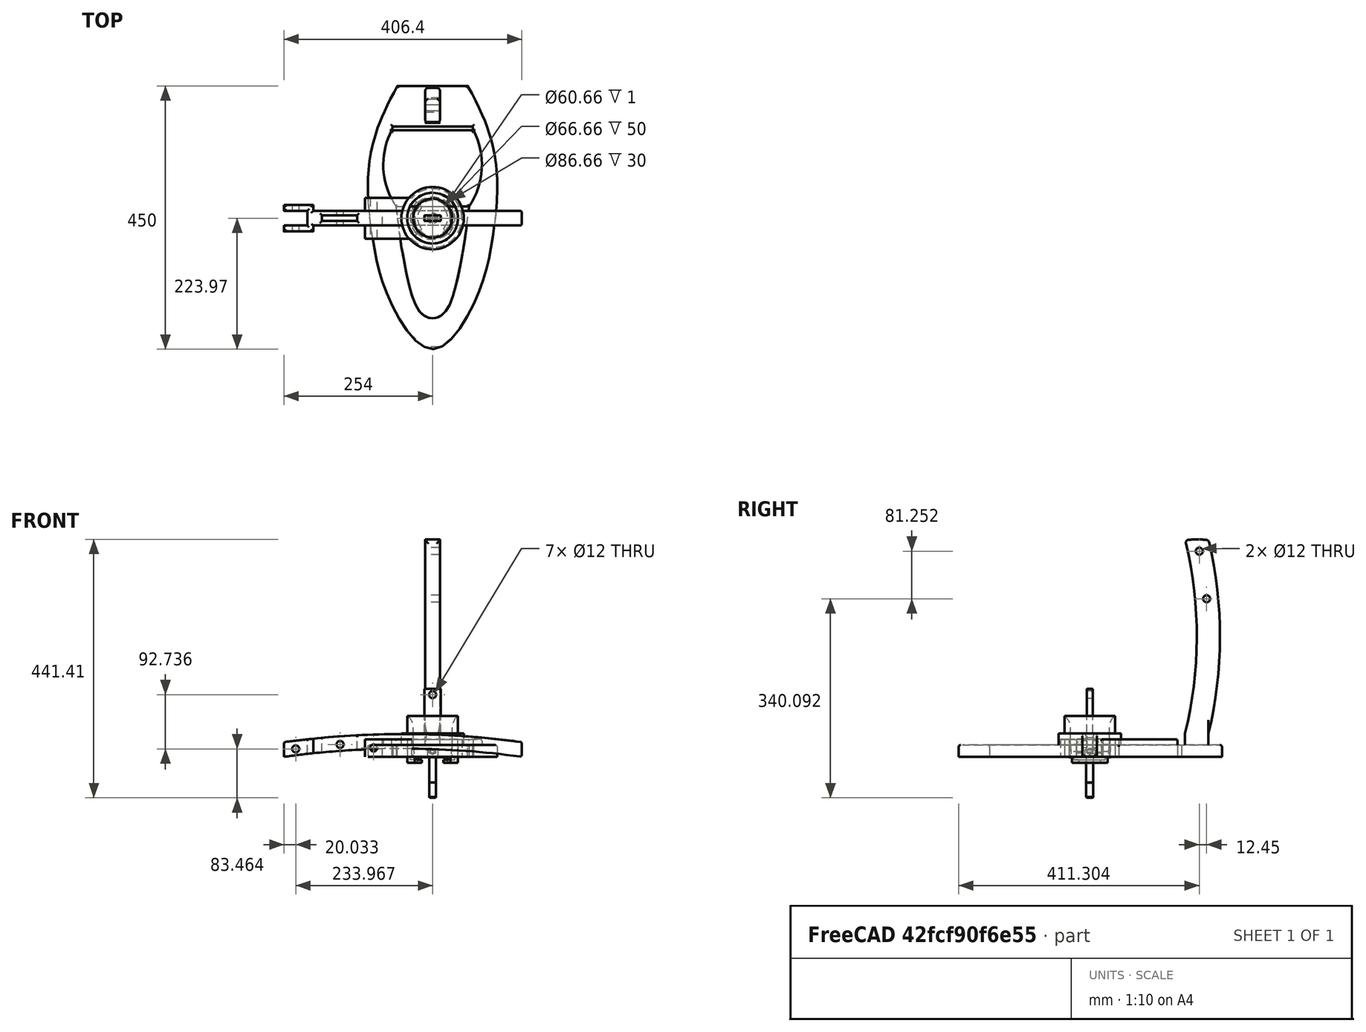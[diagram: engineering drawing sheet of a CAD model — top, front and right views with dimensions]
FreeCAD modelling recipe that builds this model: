
FCSTD DOCUMENT  (FreeCAD 1.0R39109 (Git))
Label: Espresso Machine
License: All rights reserved
LicenseURL: https://en.wikipedia.org/wiki/All_rights_reserved
objects: Sketcher::SketchObject×19, App::FeaturePython×9, PartDesign::Pad×8, App::Link×8, PartDesign::Pocket×6, PartDesign::Revolution×5, PartDesign::Body×5, PartDesign::Fillet×5, Part::FeaturePython×2, PartDesign::Mirrored×1, App::VarSet×1, App::DocumentObjectGroup×1, Assembly::JointGroup×1, Assembly::AssemblyObject×1
note: 119 computed .brp shape members not serialized (recipe doc carries the construction recipe); baked Part::Feature solids carry a one-line shape summary decoded from their .brp

FEATURE [Sketcher::SketchObject] Sketch
  ArcFitTolerance = 1e-06
  AttachmentSupport = -> [XY_Plane]
  FullyConstrained = true
  MakeInternals = false
  MapMode = 5
  sketch-geometry (2):
    g0: Circle CenterX=0 CenterY=0 CenterZ=0 NormalX=0 NormalY=0 NormalZ=1 AngleXU=0 Radius=33.33
    g1: Circle CenterX=0 CenterY=0 CenterZ=0 NormalX=0 NormalY=0 NormalZ=1 AngleXU=0 Radius=43.33
  constraints (4):
    c: Coincident(g0,g-1)
    c: Coincident(g1,g0)
    c: Diameter(g0) = 66.66
    c: Diameter(g1) = 86.66
FEATURE [PartDesign::Pad] Pad
  Direction = (0,0,1)
  Length = 50
  Length2 = 10
  Profile = -> Sketch
  ReferenceAxis = -> Sketch [N_Axis]
  Refine = true
  Suppressed = false
  Type = 0
FEATURE [Sketcher::SketchObject] Sketch001
  ArcFitTolerance = 1e-06
  AttachmentSupport = -> [XZ_Plane]
  ExternalGeometry = -> [Pad]
  FullyConstrained = true
  MakeInternals = false
  MapMode = 5
  Placement = pos=(0,0,0) rot=(1,0,0;1.5708rad)
  sketch-geometry (4):
    g0: LineSegment StartX=33.33 StartY=50 StartZ=0 EndX=43.33 EndY=50 EndZ=0
    g1: LineSegment StartX=43.33 StartY=50 StartZ=0 EndX=43.33 EndY=70 EndZ=0
    g2: ArcOfCircle CenterX=58.33 CenterY=50 CenterZ=0 NormalX=0 NormalY=0 NormalZ=1 AngleXU=0 Radius=25 StartAngle=2.2143 EndAngle=3.14159
    g3: LineSegment [constr] StartX=33.33 StartY=50 StartZ=0 EndX=33.33 EndY=0 EndZ=0
  constraints (11):
    c: Coincident(g0,g-4)
    c: Coincident(g0,g-3)
    c: Coincident(g0,g1)
    c: Vertical(g1)
    c: DistanceY(g1,g1) = 20
    c: Coincident(g2,g0)
    c: Coincident(g2,g1)
    c: Coincident(g3,g0)
    c: PointOnObject(g3,g-1)
    c: Vertical(g3)
    c: Tangent(g3,g2)
FEATURE [PartDesign::Revolution] Revolution
  Angle = 360
  Angle2 = 60
  Axis = (0,2e-16,1)
  Base = (0,0,0)
  BaseFeature = -> Pad
  Profile = -> Sketch001
  ReferenceAxis = -> Sketch001 [V_Axis]
  Refine = true
  Suppressed = false
  Type = 0
FEATURE [Sketcher::SketchObject] Sketch002
  ArcFitTolerance = 1e-06
  AttachmentSupport = -> [XZ_Plane]
  ExternalGeometry = -> [Revolution]
  FullyConstrained = true
  MakeInternals = false
  MapMode = 5
  Placement = pos=(0,0,0) rot=(1,0,0;1.5708rad)
  sketch-geometry (8):
    g0: LineSegment StartX=43.33 StartY=0 StartZ=0 EndX=43.33 EndY=-10 EndZ=0
    g1: LineSegment StartX=43.33 StartY=-10 StartZ=0 EndX=25.83 EndY=-10 EndZ=0
    g2: LineSegment StartX=25.83 StartY=-10 StartZ=0 EndX=25.83 EndY=-5 EndZ=0
    g3: LineSegment StartX=25.83 StartY=-5 StartZ=0 EndX=38.33 EndY=-5 EndZ=0
    g4: LineSegment StartX=38.33 StartY=-5 StartZ=0 EndX=38.33 EndY=0 EndZ=0
    g5: LineSegment [constr] StartX=43.33 StartY=0 StartZ=0 EndX=38.33 EndY=0 EndZ=0
    g6: LineSegment [constr] StartX=38.33 StartY=0 StartZ=0 EndX=33.33 EndY=0 EndZ=0
    g7: LineSegment StartX=38.33 StartY=0 StartZ=0 EndX=43.33 EndY=0 EndZ=0
  constraints (21):
    c: Coincident(g0,g-3)
    c: Vertical(g0)
    c: Coincident(g0,g1)
    c: Horizontal(g1)
    c: Coincident(g1,g2)
    c: Vertical(g2)
    c: Coincident(g2,g3)
    c: Coincident(g4,g3)
    c: PointOnObject(g4,g-1)
    c: Vertical(g4)
    c: Horizontal(g3)
    c: DistanceX(g1,g1) = 17.5
    c: DistanceY(g0,g0) = 10
    c: Equal(g2,g4)
    c: Coincident(g5,g0)
    c: Coincident(g5,g4)
    c: Coincident(g6,g4)
    c: Coincident(g6,g-4)
    c: Equal(g6,g5)
    c: Coincident(g7,g4)
    c: Coincident(g7,g0)
FEATURE [PartDesign::Revolution] Revolution001
  Angle = 90
  Angle2 = 60
  Axis = (0,2e-16,1)
  Base = (0,0,0)
  BaseFeature = -> Revolution
  Midplane = true
  Profile = -> Sketch002
  ReferenceAxis = -> Sketch002 [V_Axis]
  Refine = true
  Suppressed = false
  Type = 0
FEATURE [PartDesign::Mirrored] Mirrored
  BaseFeature = -> Revolution001
  MirrorPlane = -> Sketch002 [V_Axis]
  Originals = -> [Revolution001]
  Refine = true
  Suppressed = false
  TransformMode = 0
FEATURE [Sketcher::SketchObject] Sketch003
  ArcFitTolerance = 1e-06
  AttachmentSupport = -> [XZ_Plane]
  ExternalGeometry = -> [Mirrored]
  FullyConstrained = true
  MakeInternals = false
  MapMode = 5
  Placement = pos=(0,0,0) rot=(1,0,0;1.5708rad)
  sketch-geometry (5):
    g0: LineSegment StartX=36.33 StartY=0 StartZ=0 EndX=33.33 EndY=0 EndZ=0
    g1: LineSegment StartX=33.33 StartY=0 StartZ=0 EndX=30.33 EndY=0 EndZ=0
    g2: LineSegment StartX=30.33 StartY=0 StartZ=0 EndX=30.33 EndY=-1 EndZ=0
    g3: LineSegment StartX=30.33 StartY=-1 StartZ=0 EndX=36.33 EndY=-1 EndZ=0
    g4: LineSegment StartX=36.33 StartY=-1 StartZ=0 EndX=36.33 EndY=0 EndZ=0
  constraints (14):
    c: PointOnObject(g0,g-1)
    c: Coincident(g0,g-3)
    c: Coincident(g0,g1)
    c: Horizontal(g1)
    c: Coincident(g1,g2)
    c: Vertical(g2)
    c: Coincident(g2,g3)
    c: Horizontal(g3)
    c: Coincident(g3,g4)
    c: Coincident(g4,g0)
    c: Vertical(g4)
    c: Equal(g1,g0)
    c: DistanceX(g3,g3) = 6
    c: DistanceY(g4,g4) = 1
FEATURE [PartDesign::Revolution] Revolution002
  Angle = 360
  Angle2 = 60
  Axis = (0,2e-16,1)
  Base = (0,0,0)
  BaseFeature = -> Mirrored
  Midplane = true
  Profile = -> Sketch003
  ReferenceAxis = -> Sketch003 [V_Axis]
  Refine = true
  Suppressed = false
  Type = 0
FEATURE [Sketcher::SketchObject] Sketch004
  ArcFitTolerance = 1e-06
  AttachmentSupport = -> [XZ_Plane]
  ExternalGeometry = -> [Revolution002]
  FullyConstrained = true
  MakeInternals = false
  MapMode = 5
  Placement = pos=(0,0,0) rot=(1,0,0;1.5708rad)
  sketch-geometry (4):
    g0: LineSegment StartX=33.33 StartY=20 StartZ=0 EndX=53.33 EndY=20 EndZ=0
    g1: LineSegment StartX=53.33 StartY=20 StartZ=0 EndX=53.33 EndY=40 EndZ=0
    g2: LineSegment StartX=53.33 StartY=40 StartZ=0 EndX=33.33 EndY=40 EndZ=0
    g3: LineSegment StartX=33.33 StartY=40 StartZ=0 EndX=33.33 EndY=20 EndZ=0
  constraints (12):
    c: Horizontal(g0)
    c: Horizontal(g2)
    c: Vertical(g1)
    c: Vertical(g3)
    c: DistanceX(g2,g2) = 20
    c: DistanceY(g1,g1) = 20
    c: Coincident(g1,g0)
    c: Coincident(g2,g1)
    c: Coincident(g3,g2)
    c: Coincident(g3,g0)
    c: PointOnObject(g0,g-3)
    c: DistanceY(g-1,g0) = 20
FEATURE [PartDesign::Revolution] Revolution003
  Angle = 360
  Angle2 = 60
  Axis = (0,2e-16,1)
  Base = (0,0,0)
  BaseFeature = -> Revolution002
  Profile = -> Sketch004
  ReferenceAxis = -> Sketch004 [V_Axis]
  Refine = true
  Suppressed = false
  Type = 0
FEATURE [PartDesign::Body] Body  label="Pressure Vessel"
  AllowCompound = false
  Group = -> [Sketch,Pad,Sketch001,Revolution,Sketch002,Revolution001,Mirrored,Sketch003,Revolution002,Sketch004,Revolution003]
  Origin = -> Origin
  Tip = -> Revolution003
FEATURE [Sketcher::SketchObject] Sketch005
  ArcFitTolerance = 1e-06
  AttachmentSupport = -> [XY_Plane001]
  FullyConstrained = true
  MakeInternals = false
  MapMode = 5
  sketch-geometry (22):
    g0: LineSegment StartX=-60 StartY=226.026 StartZ=0 EndX=60 EndY=226.026 EndZ=0
    g1-g11: Circle [constr] x11 (B-spline internal-alignment scaffolding for g12; pole/knot coordinates omitted)
    g12: BSplineCurve PolesCount=11 KnotsCount=9 Degree=3 IsPeriodic=0
    g13-g21: GeomPoint [constr] x9 (B-spline internal-alignment scaffolding for g12; pole/knot coordinates omitted)
  constraints (15):
    c: Weight(g1) = 1
    c: Equal(g1, g2-g11) x10
    c: InternalAlignment(g1-g11 -> g12) x11
    c: InternalAlignment(g13-g21 -> g12) x9
    c: Coincident(g1,g0)
    c: PointOnObject(g6,g-2)
    c: Coincident(g11,g0)
    c: Symmetric(g19,g15,g-2)
    c: Symmetric(g18,g16,g-2)
    c: Symmetric(g20,g14,g-2)
    c: Symmetric(g10,g2,g-2)
    c: Distance(g17,g0) = 450
    c: Symmetric(g12,g12,g-2)
    c: DistanceX(g0,g0) = 120
    c: Block(g12)
FEATURE [PartDesign::Pad] Pad001
  Direction = (0,0,1)
  Length = 20
  Length2 = 10
  Profile = -> Sketch005
  ReferenceAxis = -> Sketch005 [N_Axis]
  Refine = true
  Suppressed = false
  Type = 0
FEATURE [Sketcher::SketchObject] Sketch006
  ArcFitTolerance = 1e-06
  AttachmentSupport = -> [Pad001]
  ExternalGeometry = -> [Pad001]
  FullyConstrained = true
  MakeInternals = false
  MapMode = 5
  Placement = pos=(0,0,20) rot=(0,0,1;0rad)
  sketch-geometry (8):
    g0: LineSegment StartX=-70 StartY=150 StartZ=0 EndX=70 EndY=150 EndZ=0
    g1: LineSegment StartX=-62.5 StartY=20 StartZ=0 EndX=62.5 EndY=20 EndZ=0
    g2: ArcOfCircle CenterX=42.9677 CenterY=91.301 CenterZ=0 NormalX=0 NormalY=0 NormalZ=1 AngleXU=0 Radius=127.308 StartAngle=2.66238 EndAngle=3.73606
    g3: LineSegment [constr] StartX=-109.336 StartY=82.5143 StartZ=0 EndX=-84.1287 EndY=83.9685 EndZ=0
    g4: ArcOfCircle CenterX=-42.9677 CenterY=91.301 CenterZ=0 NormalX=0 NormalY=0 NormalZ=1 AngleXU=0 Radius=127.308 StartAngle=5.68872 EndAngle=6.7624
    g5: LineSegment [constr] StartX=84.1287 StartY=83.9685 StartZ=0 EndX=109.336 EndY=82.5143 EndZ=0
    g6: LineSegment [constr] StartX=70 StartY=150 StartZ=0 EndX=95.2493 EndY=150 EndZ=0
    g7: LineSegment [constr] StartX=-70 StartY=150 StartZ=0 EndX=-95.2493 EndY=150 EndZ=0
  constraints (24):
    c: Symmetric(g0,g0,g-2)
    c: Symmetric(g1,g1,g-2)
    c: DistanceX(g0,g0) = 140
    c: DistanceX(g1,g1) = 125
    c: Distance(g-1,g0) = 150
    c: Coincident(g2,g0)
    c: Coincident(g2,g1)
    c: PointOnObject(g3,g-4)
    c: PointOnObject(g3,g2)
    c: Coincident(g4,g0)
    c: Coincident(g4,g1)
    c: PointOnObject(g5,g4)
    c: PointOnObject(g5,g-4)
    c: Symmetric(g0,g1,g5)
    c: Symmetric(g0,g1,g3)
    c: Equal(g3,g5)
    c: Coincident(g6,g0)
    c: PointOnObject(g6,g-4)
    c: Parallel(g6,g0)
    c: Equal(g6,g5)
    c: Coincident(g7,g0)
    c: PointOnObject(g7,g-4)
    c: Horizontal(g7)
    c: Distance(g-1,g1) = 20
FEATURE [PartDesign::Pad] Pad002
  BaseFeature = -> Pad001
  Direction = (0,0,1)
  Length = 10
  Length2 = 10
  Profile = -> Sketch006
  ReferenceAxis = -> Sketch006 [N_Axis]
  Refine = true
  Suppressed = false
  Type = 0
FEATURE [Sketcher::SketchObject] Sketch007
  ArcFitTolerance = 1e-06
  AttachmentSupport = -> [Pad002]
  ExternalGeometry = -> [Pad002]
  FullyConstrained = true
  MakeInternals = false
  MapMode = 5
  Placement = pos=(0,0,20) rot=(0,0,1;0rad)
  sketch-geometry (37):
    g0-g8: Circle [constr] x9 (B-spline internal-alignment scaffolding for g9; pole/knot coordinates omitted)
    g9: BSplineCurve PolesCount=9 KnotsCount=7 Degree=3 IsPeriodic=0
    g10-g16: GeomPoint [constr] x7 (B-spline internal-alignment scaffolding for g9; pole/knot coordinates omitted)
    g17: LineSegment [constr] StartX=-62.5 StartY=20 StartZ=0 EndX=-109.196 EndY=20 EndZ=0
    g18: LineSegment [constr] StartX=62.5 StartY=20 StartZ=0 EndX=109.196 EndY=20 EndZ=0
    g19: LineSegment [constr] StartX=54.2197 StartY=-43.9087 StartZ=0 EndX=100.915 EndY=-43.9087 EndZ=0
    g20: LineSegment [constr] StartX=-54.2197 StartY=-43.9087 StartZ=0 EndX=-100.915 EndY=-43.9087 EndZ=0
    g21: LineSegment [constr] StartX=49.9941 StartY=-66.9467 StartZ=0 EndX=96.6898 EndY=-66.9467 EndZ=0
    g22: LineSegment [constr] StartX=-49.9941 StartY=-66.9467 StartZ=0 EndX=-96.6898 EndY=-66.9467 EndZ=0
    g23: LineSegment [constr] StartX=-33.1368 StartY=-158.556 StartZ=0 EndX=-33.1368 EndY=-205.252 EndZ=0
    g24: LineSegment [constr] StartX=33.1368 StartY=-158.556 StartZ=0 EndX=33.1368 EndY=-205.252 EndZ=0
    g25: LineSegment [constr] StartX=0 StartY=-177.278 StartZ=0 EndX=0 EndY=-223.974 EndZ=0
    g26: LineSegment StartX=-62.5 StartY=20 StartZ=0 EndX=62.5 EndY=20 EndZ=0
    g27: LineSegment StartX=-70 StartY=150 StartZ=0 EndX=70 EndY=150 EndZ=0
    g28: LineSegment StartX=-70 StartY=150 StartZ=0 EndX=-68.2 EndY=156.718 EndZ=0
    g29: LineSegment StartX=70 StartY=150 StartZ=0 EndX=68.2 EndY=156.718 EndZ=0
    g30: LineSegment StartX=-68.2 StartY=156.718 StartZ=0 EndX=68.2 EndY=156.718 EndZ=0
    g31: LineSegment [constr] StartX=-109.196 StartY=20 StartZ=0 EndX=-100.915 EndY=-43.9087 EndZ=0
    g32: LineSegment [constr] StartX=-100.915 StartY=-43.9087 StartZ=0 EndX=-96.6898 EndY=-66.9467 EndZ=0
    g33: LineSegment [constr] StartX=109.196 StartY=20 StartZ=0 EndX=100.915 EndY=-43.9087 EndZ=0
    g34: LineSegment [constr] StartX=100.915 StartY=-43.9087 StartZ=0 EndX=96.6898 EndY=-66.9467 EndZ=0
    g35: LineSegment [constr] StartX=33.1368 StartY=-205.252 StartZ=0 EndX=0 EndY=-223.974 EndZ=0
    g36: LineSegment [constr] StartX=-33.1368 StartY=-205.252 StartZ=0 EndX=0 EndY=-223.974 EndZ=0
  constraints (66):
    c: Weight(g0) = 1
    c: Equal(g0, g1-g8) x8
    c: InternalAlignment(g0-g8 -> g9) x9
    c: InternalAlignment(g10-g16 -> g9) x7
    c: Coincident(g0,g-5)
    c: PointOnObject(g4,g-2)
    c: Coincident(g8,g-4)
    c: Symmetric(g11,g15,g-2)
    c: Symmetric(g12,g14,g-2)
    c: Symmetric(g7,g1,g-2)
    c: Coincident(g17,g9)
    c: PointOnObject(g17,g-6)
    c: Horizontal(g17)
    c: Coincident(g18,g9)
    c: PointOnObject(g18,g-6)
    c: Coincident(g19,g7)
    c: PointOnObject(g19,g-6)
    c: Coincident(g20,g1)
    c: PointOnObject(g20,g-6)
    c: Coincident(g21,g15)
    c: PointOnObject(g21,g-6)
    c: Coincident(g22,g11)
    c: PointOnObject(g22,g-6)
    c: Coincident(g23,g3)
    c: PointOnObject(g23,g-6)
    c: Coincident(g24,g5)
    c: PointOnObject(g24,g-6)
    c: Coincident(g25,g4)
    c: PointOnObject(g25,g-6)
    c: Vertical(g25)
    c: Equal(g23,g22)
    c: Equal(g22,g20)
    c: Equal(g20,g17)
    c: Equal(g18,g19)
    c: Equal(g19,g21)
    c: Equal(g21,g24)
    c: Equal(g23,g25)
    c: Equal(g24,g25)
    c: Parallel(g24,g23)
    c: Parallel(g22,g21)
    c: Coincident(g27,g-7)
    c: Coincident(g27,g-7)
    c: Coincident(g28,g27)
    c: Coincident(g29,g27)
    c: Coincident(g30,g28)
    c: Coincident(g30,g29)
    c: Horizontal(g30)
    c: Angle(g29,g27) = 1.309
    c: Angle(g27,g28) = 1.309
    c: Coincident(g26,g0)
    c: Coincident(g26,g8)
    c: Parallel(g19,g21)
    c: Coincident(g31,g17)
    c: Coincident(g31,g20)
    c: Coincident(g32,g20)
    c: Coincident(g32,g22)
    c: Coincident(g33,g18)
    c: Coincident(g33,g19)
    c: Coincident(g34,g19)
    c: Coincident(g34,g21)
    c: Coincident(g35,g24)
    c: Coincident(g35,g25)
    c: Coincident(g36,g23)
    c: Coincident(g36,g25)
    c: Block(g9)
    c: DistanceX(g30,g30) = 136.4
FEATURE [PartDesign::Pocket] Pocket
  BaseFeature = -> Pad002
  Direction = (0,0,-1)
  Length = 5
  Length2 = 5
  Profile = -> Sketch007
  ReferenceAxis = -> Sketch007 [N_Axis]
  Refine = true
  Suppressed = false
  Type = 1
FEATURE [PartDesign::Fillet] Fillet
  Base = -> Pocket [Edge30,Edge27,Edge6,Edge4,Edge14,Edge16,Edge18,Edge31,Edge32,Edge17]
  BaseFeature = -> Pocket
  Radius = 3
  Refine = true
  SupportTransform = false
  Suppressed = false
  UseAllEdges = false
FEATURE [Sketcher::SketchObject] Sketch008
  ArcFitTolerance = 1e-06
  AttachmentSupport = -> [Fillet]
  ExternalGeometry = -> [Fillet]
  FullyConstrained = true
  MakeInternals = false
  MapMode = 5
  Placement = pos=(0,0,20) rot=(0,0,1;0rad)
  sketch-geometry (4):
    g0: LineSegment StartX=-12.5 StartY=203.026 StartZ=0 EndX=-12.5 EndY=163.026 EndZ=0
    g1: LineSegment StartX=-12.5 StartY=163.026 StartZ=0 EndX=12.5 EndY=163.026 EndZ=0
    g2: LineSegment StartX=12.5 StartY=163.026 StartZ=0 EndX=12.5 EndY=203.026 EndZ=0
    g3: LineSegment StartX=12.5 StartY=203.026 StartZ=0 EndX=-12.5 EndY=203.026 EndZ=0
  constraints (11):
    c: Coincident(g0,g1)
    c: Coincident(g1,g2)
    c: Coincident(g2,g3)
    c: Coincident(g3,g0)
    c: Vertical(g0)
    c: Vertical(g2)
    c: Horizontal(g3)
    c: Symmetric(g1,g0,g-2)
    c: Distance(g-3,g3) = 20
    c: DistanceX(g3,g3) = 25
    c: DistanceY(g2,g2) = 40
FEATURE [PartDesign::Pad] Pad003
  BaseFeature = -> Fillet
  Direction = (0,0,1)
  Length = 20
  Length2 = 10
  Profile = -> Sketch008
  ReferenceAxis = -> Sketch008 [N_Axis]
  Refine = true
  Suppressed = false
  Type = 0
FEATURE [Sketcher::SketchObject] Sketch009
  ArcFitTolerance = 1e-06
  AttachmentSupport = -> [YZ_Plane001]
  ExternalGeometry = -> [Pad003]
  FullyConstrained = true
  MakeInternals = false
  MapMode = 5
  Placement = pos=(0,0,0) rot=(0.57735,0.57735,0.57735;2.0944rad)
  sketch-geometry (5):
    g0: ArcOfCircle CenterX=-483.424 CenterY=205.1 CenterZ=0 NormalX=0 NormalY=0 NormalZ=1 AngleXU=0 Radius=706.025 StartAngle=6.04716 EndAngle=6.51922
    g1: ArcOfCircle CenterX=-508.424 CenterY=205.1 CenterZ=0 NormalX=0 NormalY=0 NormalZ=1 AngleXU=0 Radius=691.45 StartAngle=6.04208 EndAngle=6.52429
    g2: LineSegment [constr] StartX=183.026 StartY=205.1 StartZ=0 EndX=222.602 EndY=205.1 EndZ=0
    g3: LineSegment StartX=163.026 StartY=40 StartZ=0 EndX=203.026 EndY=40 EndZ=0
    g4: ArcOfCircle CenterX=183.026 CenterY=205.1 CenterZ=0 NormalX=0 NormalY=0 NormalZ=1 AngleXU=0 Radius=166.307 StartAngle=1.45025 EndAngle=1.69135
  constraints (15):
    c: Coincident(g0,g-3)
    c: Coincident(g1,g-3)
    c: Horizontal(g0,g1)
    c: DistanceX(g1,g0) = 25
    c: DistanceY(g0,g0) = 330.2
    c: DistanceY(g1,g1) = 330.2
    c: PointOnObject(g2,g1)
    c: PointOnObject(g2,g0)
    c: Horizontal(g2)
    c: Coincident(g3,g1)
    c: Coincident(g3,g0)
    c: Coincident(g4,g2)
    c: Coincident(g4,g1)
    c: Coincident(g0,g4)
    c: Symmetric(g1,g1,g2)
FEATURE [PartDesign::Pad] Pad004
  BaseFeature = -> Pad003
  Direction = (1,0,0)
  Length = 25
  Length2 = 10
  Midplane = true
  Profile = -> Sketch009
  ReferenceAxis = -> Sketch009 [N_Axis]
  Refine = true
  Suppressed = false
  Type = 0
FEATURE [PartDesign::Fillet] Fillet001
  Base = -> Pad004 [Edge70,Edge67,Edge69,Edge68,Edge72,Edge71]
  BaseFeature = -> Pad004
  Radius = 5
  Refine = true
  SupportTransform = false
  Suppressed = false
  UseAllEdges = false
FEATURE [Sketcher::SketchObject] Sketch010
  ArcFitTolerance = 1e-06
  AttachmentSupport = -> [Fillet001]
  ExternalGeometry = -> [Fillet001]
  FullyConstrained = true
  MakeInternals = false
  MapMode = 5
  Placement = pos=(-12.5,0,0) rot=(0.57735,-0.57735,-0.57735;2.0944rad)
  sketch-geometry (6):
    g0: Circle CenterX=-187.334 CenterY=351.344 CenterZ=0 NormalX=0 NormalY=0 NormalZ=1 AngleXU=0 Radius=6
    g1: Circle CenterX=-199.784 CenterY=270.092 CenterZ=0 NormalX=0 NormalY=0 NormalZ=1 AngleXU=0 Radius=6
    g2: LineSegment [constr] StartX=-187.334 StartY=351.344 StartZ=0 EndX=-168.24 EndY=347.33 EndZ=0
    g3: LineSegment [constr] StartX=-199.784 StartY=270.092 StartZ=0 EndX=-180.133 EndY=268.289 EndZ=0
    g4: LineSegment [constr] StartX=-199.784 StartY=270.092 StartZ=0 EndX=-219.435 EndY=271.895 EndZ=0
    g5: LineSegment [constr] StartX=-187.334 StartY=351.344 StartZ=0 EndX=-206.427 EndY=355.357 EndZ=0
  constraints (18):
    c: Diameter(g0) = 12
    c: Distance(g0,g-3) = 20
    c: Diameter(g1) = 12
    c: Distance(g0,g1) = 76.2
    c: Coincident(g2,g0)
    c: PointOnObject(g2,g-5)
    c: Coincident(g4,g1)
    c: PointOnObject(g4,g-4)
    c: Coincident(g5,g0)
    c: PointOnObject(g5,g-4)
    c: Equal(g4,g3)
    c: Equal(g2,g5)
    c: Coincident(g3,g1)
    c: PointOnObject(g3,g-5)
    c: Parallel(g3,g4)
    c: Perpendicular(g-5,g3)
    c: Perpendicular(g-5,g2)
    c: Parallel(g2,g5)
FEATURE [PartDesign::Pocket] Pocket001
  BaseFeature = -> Fillet001
  Direction = (1,0,0)
  Length = 5
  Length2 = 5
  Profile = -> Sketch010
  ReferenceAxis = -> Sketch010 [N_Axis]
  Refine = true
  Suppressed = false
  Type = 1
FEATURE [PartDesign::Body] Body001  label="Stand"
  AllowCompound = false
  Group = -> [Sketch005,Pad001,Sketch006,Pad002,Sketch007,Pocket,Fillet,Sketch008,Pad003,Sketch009,Pad004,Fillet001,Sketch010,Pocket001]
  Origin = -> Origin001
  Tip = -> Pocket001
FEATURE [Sketcher::SketchObject] Sketch011
  ArcFitTolerance = 1e-06
  AttachmentSupport = -> [XY_Plane002]
  FullyConstrained = true
  MakeInternals = false
  MapMode = 5
  expr: Constraints[43] = VarSet.Plunger_Clearance_Length * 2
  expr: Constraints[45] = VarSet.Plunger_Clearance_Length / 2
  sketch-geometry (16):
    g0: LineSegment StartX=-214 StartY=-12.5 StartZ=0 EndX=-214 EndY=12.5 EndZ=0
    g1: LineSegment StartX=-214 StartY=12.5 StartZ=0 EndX=-254 EndY=12.5 EndZ=0
    g2: LineSegment StartX=-254 StartY=12.5 StartZ=0 EndX=-254 EndY=22.5 EndZ=0
    g3: LineSegment StartX=152.4 StartY=12.5 StartZ=0 EndX=152.4 EndY=-12.5 EndZ=0
    g4: LineSegment StartX=-254 StartY=-22.5 StartZ=0 EndX=-254 EndY=-12.5 EndZ=0
    g5: LineSegment StartX=-254 StartY=-12.5 StartZ=0 EndX=-214 EndY=-12.5 EndZ=0
    g6: LineSegment StartX=-254 StartY=22.5 StartZ=0 EndX=-204 EndY=22.5 EndZ=0
    g7: LineSegment StartX=-204 StartY=22.5 StartZ=0 EndX=-204 EndY=12.5 EndZ=0
    g8: LineSegment StartX=-204 StartY=12.5 StartZ=0 EndX=152.4 EndY=12.5 EndZ=0
    g9: LineSegment StartX=-254 StartY=-22.5 StartZ=0 EndX=-204 EndY=-22.5 EndZ=0
    g10: LineSegment StartX=-204 StartY=-22.5 StartZ=0 EndX=-204 EndY=-12.5 EndZ=0
    g11: LineSegment StartX=-204 StartY=-12.5 StartZ=0 EndX=152.4 EndY=-12.5 EndZ=0
    g12: LineSegment StartX=-189 StartY=5 StartZ=0 EndX=-189 EndY=-5 EndZ=0
    g13: LineSegment StartX=-189 StartY=-5 StartZ=0 EndX=-129 EndY=-5 EndZ=0
    g14: LineSegment StartX=-129 StartY=-5 StartZ=0 EndX=-129 EndY=5 EndZ=0
    g15: LineSegment StartX=-129 StartY=5 StartZ=0 EndX=-189 EndY=5 EndZ=0
  constraints (46):
    c: Coincident(g0,g1)
    c: Horizontal(g1)
    c: Coincident(g1,g2)
    c: Vertical(g2)
    c: Vertical(g4)
    c: Coincident(g4,g5)
    c: Coincident(g5,g0)
    c: Horizontal(g5)
    c: Equal(g2,g4)
    c: Symmetric(g3,g3,g-1)
    c: DistanceY(g0,g0) = 25
    c: DistanceX(g1,g1) = 40
    c: Equal(g1,g5)
    c: Symmetric(g0,g0,g-1)
    c: DistanceY(g2,g2) = 10
    c: Coincident(g2,g6)
    c: Horizontal(g6)
    c: Coincident(g6,g7)
    c: Vertical(g7)
    c: Coincident(g7,g8)
    c: Horizontal(g8)
    c: Coincident(g4,g9)
    c: Horizontal(g9)
    c: Coincident(g9,g10)
    c: Vertical(g10)
    c: Coincident(g10,g11)
    c: Horizontal(g11)
    c: Vertical(g11,g8)
    c: Vertical(g7,g10)
    c: Equal(g7,g10)
    c: Horizontal(g0,g7)
    c: DistanceX(g0,g7) = 10
    c: DistanceX(g2,g3) = 406.4
    c: Coincident(g8,g3)
    c: Distance(g3,g-2) = 152.4
    c: Coincident(g12,g13)
    c: Coincident(g13,g14)
    c: Coincident(g14,g15)
    c: Coincident(g15,g12)
    c: Vertical(g12)
    c: Horizontal(g13)
    c: Horizontal(g15)
    c: Symmetric(g14,g13,g-1)
    c: DistanceX(g15,g15) = 60
    c: Distance(g14,g14) = 10
    c: DistanceX(g7,g12) = 15
FEATURE [PartDesign::Pad] Pad005
  Direction = (0,0,1)
  Length = 40
  Length2 = 10
  Profile = -> Sketch011
  ReferenceAxis = -> Sketch011 [N_Axis]
  Refine = true
  Suppressed = false
  Type = 0
FEATURE [Sketcher::SketchObject] Sketch012
  ArcFitTolerance = 1e-06
  AttachmentSupport = -> [Pad005]
  ExternalGeometry = -> [Pad005]
  FullyConstrained = true
  MakeInternals = false
  MapMode = 5
  Placement = pos=(0,-12.5,0) rot=(1,0,0;1.5708rad)
  sketch-geometry (6):
    g0: ArcOfCircle CenterX=-50.8 CenterY=-1468.03 CenterZ=0 NormalX=0 NormalY=0 NormalZ=1 AngleXU=0 Radius=1482.03 StartAngle=1.43325 EndAngle=1.70834
    g1: ArcOfCircle CenterX=-50.8 CenterY=-1468.03 CenterZ=0 NormalX=0 NormalY=0 NormalZ=1 AngleXU=0 Radius=1506.8 StartAngle=1.43553 EndAngle=1.70606
    g2: LineSegment StartX=-254 StartY=2.274e-13 StartZ=0 EndX=152.4 EndY=-2.274e-13 EndZ=0
    g3: LineSegment StartX=-254 StartY=25 StartZ=0 EndX=-254 EndY=40 EndZ=0
    g4: LineSegment StartX=152.4 StartY=40 StartZ=0 EndX=152.4 EndY=25 EndZ=0
    g5: LineSegment StartX=-254 StartY=40 StartZ=0 EndX=152.4 EndY=40 EndZ=0
  constraints (15):
    c: Coincident(g0,g-5)
    c: Coincident(g0,g-6)
    c: PointOnObject(g1,g-5)
    c: PointOnObject(g1,g-6)
    c: Coincident(g1,g0)
    c: DistanceY(g0,g1) = 25
    c: Coincident(g2,g0)
    c: Coincident(g2,g0)
    c: Coincident(g3,g1)
    c: Coincident(g3,g-9)
    c: Coincident(g4,g-8)
    c: Coincident(g4,g1)
    c: Coincident(g5,g3)
    c: Coincident(g5,g4)
    c: Radius(g0) = 1482.03
FEATURE [PartDesign::Pocket] Pocket002
  BaseFeature = -> Pad005
  Direction = (0,1,-2e-16)
  Length = 5
  Length2 = 5
  Midplane = true
  Profile = -> Sketch012
  ReferenceAxis = -> Sketch012 [N_Axis]
  Refine = true
  Suppressed = false
  Type = 1
FEATURE [PartDesign::Fillet] Fillet002
  Base = -> Pocket002 [Face14,Face4]
  BaseFeature = -> Pocket002
  Radius = 3
  Refine = true
  SupportTransform = false
  Suppressed = false
  UseAllEdges = false
FEATURE [Sketcher::SketchObject] Sketch013
  ArcFitTolerance = 1e-06
  AttachmentSupport = -> [Fillet002]
  ExternalGeometry = -> [Fillet002]
  FullyConstrained = true
  MakeInternals = false
  MapMode = 5
  Placement = pos=(0,-12.5,0) rot=(1,0,0;1.5708rad)
  sketch-geometry (6):
    g0: Circle CenterX=-158.2 CenterY=21.0121 CenterZ=0 NormalX=0 NormalY=0 NormalZ=1 AngleXU=0 Radius=6
    g1: Circle CenterX=-233.967 CenterY=13.4636 CenterZ=0 NormalX=0 NormalY=0 NormalZ=1 AngleXU=0 Radius=6
    g2: LineSegment [constr] StartX=-159.034 StartY=31.8641 StartZ=0 EndX=-158.2 EndY=21.0121 EndZ=0
    g3: LineSegment [constr] StartX=-158.2 StartY=21.0121 StartZ=0 EndX=-157.366 EndY=10.1601 EndZ=0
    g4: LineSegment [constr] StartX=-254 StartY=21.9723 StartZ=0 EndX=-214 EndY=4.98325 EndZ=0
    g5: LineSegment [constr] StartX=-214 StartY=26.8823 StartZ=0 EndX=-254 EndY=2.238e-13 EndZ=0
  constraints (15):
    c: Diameter(g0) = 12
    c: Diameter(g1) = 12
    c: Symmetric(g-9,g-8,g2)
    c: Coincident(g0,g2)
    c: Coincident(g0,g3)
    c: Parallel(g3,g2)
    c: Equal(g2,g3)
    c: Coincident(g4,g-4)
    c: Coincident(g4,g-11)
    c: Coincident(g5,g-5)
    c: Coincident(g5,g-11)
    c: PointOnObject(g1,g4)
    c: PointOnObject(g1,g5)
    c: PointOnObject(g2,g-8)
    c: PointOnObject(g3,g-7)
FEATURE [App::VarSet] VarSet
  Plunger_Clearance_Length = 30
FEATURE [PartDesign::Pocket] Pocket003
  BaseFeature = -> Fillet002
  Direction = (0,1,-2e-16)
  Length = 5
  Length2 = 5
  Midplane = true
  Profile = -> Sketch013
  ReferenceAxis = -> Sketch013 [N_Axis]
  Refine = true
  Suppressed = false
  Type = 1
FEATURE [PartDesign::Body] Body002  label="Presure Lever"
  AllowCompound = false
  Group = -> [Sketch011,Pad005,Sketch012,Pocket002,Fillet002,Sketch013,Pocket003]
  Origin = -> Origin002
  Tip = -> Pocket003
FEATURE [Sketcher::SketchObject] Sketch014
  ArcFitTolerance = 1e-06
  AttachmentSupport = -> [XY_Plane003]
  FullyConstrained = true
  MakeInternals = false
  MapMode = 5
  expr: Constraints[20] = VarSet.Plunger_Clearance_Length + 12.45 mm
  sketch-geometry (9):
    g0: LineSegment StartX=-85.78 StartY=-12.5 StartZ=0 EndX=-85.78 EndY=12.5 EndZ=0
    g1: LineSegment StartX=-85.78 StartY=12.5 StartZ=0 EndX=-115.78 EndY=12.5 EndZ=0
    g2: LineSegment StartX=-115.78 StartY=12.5 StartZ=0 EndX=-115.78 EndY=34.9255 EndZ=0
    g3: LineSegment StartX=-115.78 StartY=34.9255 StartZ=0 EndX=-35.78 EndY=34.9255 EndZ=0
    g4: LineSegment StartX=-35.78 StartY=-34.9255 StartZ=0 EndX=-115.78 EndY=-34.9255 EndZ=0
    g5: LineSegment StartX=-115.78 StartY=-34.9255 StartZ=0 EndX=-115.78 EndY=-12.5 EndZ=0
    g6: LineSegment StartX=-115.78 StartY=-12.5 StartZ=0 EndX=-85.78 EndY=-12.5 EndZ=0
    g7: ArcOfCircle CenterX=0 CenterY=1.8e-15 CenterZ=0 NormalX=0 NormalY=0 NormalZ=1 AngleXU=0 Radius=50 StartAngle=3.91491 EndAngle=8.65146
    g8: Circle CenterX=0 CenterY=1.8e-15 CenterZ=0 NormalX=0 NormalY=0 NormalZ=1 AngleXU=0 Radius=43.33
  constraints (26):
    c: Vertical(g0)
    c: Coincident(g0,g1)
    c: Horizontal(g1)
    c: Coincident(g1,g2)
    c: Vertical(g2)
    c: Coincident(g2,g3)
    c: Horizontal(g3)
    c: Horizontal(g4)
    c: Coincident(g4,g5)
    c: Vertical(g5)
    c: Coincident(g5,g6)
    c: Coincident(g6,g0)
    c: Horizontal(g6)
    c: Equal(g2,g5)
    c: Equal(g1,g6)
    c: Coincident(g7,g3)
    c: Coincident(g7,g4)
    c: Radius(g7) = 50
    c: Coincident(g8,g7)
    c: Diameter(g8) = 86.66
    c: Distance(g8,g0) = 42.45
    c: Symmetric(g3,g4,g-1)
    c: Coincident(g7,g-1)
    c: DistanceY(g0,g0) = 25
    c: DistanceX(g1,g1) = 30
    c: DistanceX(g3,g3) = 80
FEATURE [PartDesign::Pad] Pad006
  Direction = (0,0,1)
  Length = 30
  Length2 = 10
  Profile = -> Sketch014
  ReferenceAxis = -> Sketch014 [N_Axis]
  Refine = true
  Suppressed = false
  Type = 0
FEATURE [Sketcher::SketchObject] Sketch015
  ArcFitTolerance = 1e-06
  AttachmentSupport = -> [Pad006]
  ExternalGeometry = -> [Pad006]
  FullyConstrained = true
  MakeInternals = false
  MapMode = 5
  Placement = pos=(0,-34.9255,0) rot=(1,0,0;1.5708rad)
  sketch-geometry (3):
    g0: Circle CenterX=-100.78 CenterY=15 CenterZ=0 NormalX=0 NormalY=0 NormalZ=1 AngleXU=0 Radius=6
    g1: LineSegment [constr] StartX=-100.78 StartY=15 StartZ=0 EndX=-100.78 EndY=0 EndZ=0
    g2: LineSegment [constr] StartX=-100.78 StartY=15 StartZ=0 EndX=-100.78 EndY=30 EndZ=0
  constraints (9):
    c: Diameter(g0) = 12
    c: Distance(g0,g-4) = 15
    c: Coincident(g1,g0)
    c: PointOnObject(g1,g-5)
    c: Vertical(g1)
    c: Coincident(g2,g0)
    c: PointOnObject(g2,g-3)
    c: Vertical(g2)
    c: Equal(g2,g1)
FEATURE [PartDesign::Pocket] Pocket004
  BaseFeature = -> Pad006
  Direction = (0,1,-2e-16)
  Length = 5
  Length2 = 5
  Profile = -> Sketch015
  ReferenceAxis = -> Sketch015 [N_Axis]
  Refine = true
  Suppressed = false
  Type = 1
FEATURE [PartDesign::Body] Body003  label="Vessel Holder"
  AllowCompound = false
  Group = -> [Sketch014,Pad006,Sketch015,Pocket004]
  Origin = -> Origin003
  Tip = -> Pocket004
FEATURE [Sketcher::SketchObject] Sketch016
  ArcFitTolerance = 1e-06
  AttachmentSupport = -> [YZ_Plane004]
  FullyConstrained = true
  MakeInternals = false
  MapMode = 5
  Placement = pos=(0,0,0) rot=(0.57735,0.57735,0.57735;2.0944rad)
  sketch-geometry (6):
    g0: LineSegment StartX=0 StartY=40 StartZ=0 EndX=33.33 EndY=40 EndZ=0
    g1: LineSegment StartX=33.33 StartY=40 StartZ=0 EndX=33.33 EndY=20 EndZ=0
    g2: LineSegment StartX=31.8 StartY=1.61e-14 StartZ=0 EndX=0 EndY=0 EndZ=0
    g3: ArcOfCircle CenterX=163.284 CenterY=1.61e-14 CenterZ=0 NormalX=0 NormalY=0 NormalZ=1 AngleXU=0 Radius=131.484 StartAngle=2.98889 EndAngle=3.14159
    g4: LineSegment StartX=0 StartY=40 StartZ=0 EndX=0 EndY=0 EndZ=0
    g5: LineSegment [constr] StartX=31.8 StartY=1.61e-14 StartZ=0 EndX=163.284 EndY=1.61e-14 EndZ=0
  constraints (17):
    c: PointOnObject(g0,g-2)
    c: Horizontal(g0)
    c: Coincident(g0,g1)
    c: Vertical(g1)
    c: PointOnObject(g2,g-1)
    c: Coincident(g2,g-1)
    c: Coincident(g3,g1)
    c: Coincident(g3,g2)
    c: DistanceX(g0,g0) = 33.33
    c: Coincident(g4,g0)
    c: Coincident(g4,g2)
    c: DistanceY(g4,g4) = 40
    c: DistanceY(g1,g1) = 20
    c: DistanceX(g2,g2) = 31.8
    c: Coincident(g5,g2)
    c: Coincident(g5,g3)
    c: Horizontal(g5)
FEATURE [PartDesign::Revolution] Revolution004
  Angle = 360
  Angle2 = 60
  Axis = (0,0,1)
  Base = (0,0,0)
  Placement = pos=(0,0,0) rot=(1,1,1;2.0944rad)
  Profile = -> Sketch016
  ReferenceAxis = -> Sketch016 [V_Axis]
  Refine = true
  Reversed = true
  Suppressed = false
  Type = 0
FEATURE [Sketcher::SketchObject] Sketch017
  ArcFitTolerance = 1e-06
  AttachmentSupport = -> [Revolution004]
  FullyConstrained = true
  MakeInternals = false
  MapMode = 5
  Placement = pos=(-8.8e-15,0,40) rot=(0,0,-1;1.5708rad)
  expr: Constraints[8] = VarSet.Plunger_Clearance_Length - 2.5 mm
  sketch-geometry (4):
    g0: LineSegment StartX=-4.995 StartY=13.75 StartZ=0 EndX=-4.995 EndY=-13.75 EndZ=0
    g1: LineSegment StartX=-4.995 StartY=-13.75 StartZ=0 EndX=4.995 EndY=-13.75 EndZ=0
    g2: LineSegment StartX=4.995 StartY=-13.75 StartZ=0 EndX=4.995 EndY=13.75 EndZ=0
    g3: LineSegment StartX=4.995 StartY=13.75 StartZ=0 EndX=-4.995 EndY=13.75 EndZ=0
  constraints (10):
    c: Coincident(g0,g1)
    c: Coincident(g1,g2)
    c: Coincident(g2,g3)
    c: Coincident(g3,g0)
    c: Vertical(g0)
    c: Horizontal(g1)
    c: Symmetric(g0,g2,g-2)
    c: Symmetric(g2,g1,g-1)
    c: DistanceY(g2,g2) = 27.5
    c: Distance(g3,g3) = 9.99
FEATURE [PartDesign::Pad] Pad007
  BaseFeature = -> Revolution004
  Direction = (0,0,1)
  Length = 76.2
  Length2 = 10
  Placement = pos=(0,0,0) rot=(1,1,1;2.0944rad)
  Profile = -> Sketch017
  ReferenceAxis = -> Sketch017 [N_Axis]
  Refine = true
  Suppressed = false
  Type = 0
FEATURE [Sketcher::SketchObject] Sketch018
  ArcFitTolerance = 1e-06
  AttachmentSupport = -> [Pad007]
  ExternalGeometry = -> [Pad007]
  FullyConstrained = true
  MakeInternals = false
  MapMode = 5
  Placement = pos=(0,-4.995,0) rot=(0.57735,0.57735,-0.57735;2.0944rad)
  sketch-geometry (1):
    g0: Circle CenterX=-106.2 CenterY=0 CenterZ=0 NormalX=0 NormalY=0 NormalZ=1 AngleXU=0 Radius=6
  constraints (3):
    c: PointOnObject(g0,g-1)
    c: Diameter(g0) = 12
    c: Distance(g0,g-3) = 10
FEATURE [PartDesign::Pocket] Pocket005
  BaseFeature = -> Pad007
  Direction = (0,1,0)
  Length = 5
  Length2 = 5
  Placement = pos=(0,0,0) rot=(1,1,1;2.0944rad)
  Profile = -> Sketch018
  ReferenceAxis = -> Sketch018 [N_Axis]
  Refine = true
  Suppressed = false
  Type = 1
FEATURE [PartDesign::Fillet] Fillet003
  Base = -> Pocket005 [Face8,Edge15,Edge8,Edge10,Edge12]
  BaseFeature = -> Pocket005
  Placement = pos=(0,0,0) rot=(1,1,1;2.0944rad)
  Radius = 1
  Refine = true
  SupportTransform = false
  Suppressed = false
  UseAllEdges = false
FEATURE [PartDesign::Fillet] Fillet004
  Base = -> Fillet003 [Edge28,Edge47]
  BaseFeature = -> Fillet003
  Placement = pos=(0,0,0) rot=(1,1,1;2.0944rad)
  Radius = 1
  Refine = true
  SupportTransform = false
  Suppressed = false
  UseAllEdges = false
FEATURE [PartDesign::Body] Body004  label="Plunger"
  AllowCompound = false
  Group = -> [Sketch016,Revolution004,Sketch017,Pad007,Sketch018,Pocket005,Fillet003,Fillet004]
  Origin = -> Origin004
  Tip = -> Fillet004
FEATURE [Part::FeaturePython] Screw  label="M12x45-Screw"  # WARN: FeaturePython — macro-defined, semantics opaque (R4)
  Diameter = 9
  Invert = false
  LeftHanded = false
  Length = 16
  LengthCustom = 45
  MatchOuter = false
  OffsetAngle = 0
  Thread = false
  Type = 53
FEATURE [Part::FeaturePython] Screw001  label="M12x70-Screw"  # WARN: FeaturePython — macro-defined, semantics opaque (R4)
  Diameter = 9
  Invert = false
  LeftHanded = false
  Length = 16
  LengthCustom = 70
  MatchOuter = false
  OffsetAngle = 0
  Thread = false
  Type = 53
FEATURE [App::DocumentObjectGroup] Group  label="Bolts "
  Group = -> [Screw,Screw001]
FEATURE [App::Link] Stand  label="Stand001"
  LinkedObject = -> Body001
FEATURE [App::FeaturePython] GroundedJoint  # Assembly grounded joint (typed FeaturePython)
  ObjectToGround = -> Stand
FEATURE [App::Link] Pressure_Vessel  label="Pressure Vessel001"
  LinkPlacement = pos=(-7.405,97.5046,283.87) rot=(-0.090686,0.090686,0.991742;1.57909rad)
  LinkedObject = -> Body
  Placement = pos=(-7.405,97.5046,283.87) rot=(-0.090686,0.090686,0.991742;1.57909rad)
FEATURE [App::Link] Vessel_Holder  label="Vessel Holder001"
  LinkPlacement = pos=(-7.405,95.6909,274.036) rot=(0.084273,0.090738,0.992303;4.63084rad)
  LinkedObject = -> Body003
  Placement = pos=(-7.405,95.6909,274.036) rot=(0.084273,0.090738,0.992303;4.63084rad)
FEATURE [App::Link] Plunger  label="Plunger001"
  LinkPlacement = pos=(-7.405,92.7875,258.293) rot=(-0.090686,0.090686,0.991742;1.57909rad)
  LinkedObject = -> Body004
  Placement = pos=(-7.405,92.7875,258.293) rot=(-0.090686,0.090686,0.991742;1.57909rad)
FEATURE [App::Link] M12x45_Screw001  label="M12x45-Screw002"
  LinkPlacement = pos=(-12.015,112.049,362.732) rot=(0.090686,0.991742,-0.090686;4.7041rad)
  LinkedObject = -> Screw
  Placement = pos=(-12.015,112.049,362.732) rot=(0.090686,0.991742,-0.090686;4.7041rad)
FEATURE [App::Link] M6x70_Screw  label="M6x70-Screw001"
  LinkPlacement = pos=(34,187.334,351.344) rot=(0.612372,-0.500001,0.612372;4.06889rad)
  LinkedObject = -> Screw001
  Placement = pos=(34,187.334,351.344) rot=(0.612372,-0.500001,0.612372;4.06889rad)
FEATURE [App::Link] M6x70_Screw001  label="M6x70-Screw002"
  LinkPlacement = pos=(34,199.784,270.092) rot=(0.609376,-0.507269,0.609376;4.08048rad)
  LinkedObject = -> Screw001
  Placement = pos=(34,199.784,270.092) rot=(0.609376,-0.507269,0.609376;4.08048rad)
FEATURE [App::FeaturePython] Joint  label="Revolute"  # Assembly joint (typed FeaturePython)
  Activated = true
  AngleMax = 0
  AngleMin = 0
  Detach1 = false
  Detach2 = false
  Distance = 0
  Distance2 = 0
  EnableAngleMax = false
  EnableAngleMin = false
  EnableLengthMax = false
  EnableLengthMin = false
  JointType = 1 (Revolute)
  LengthMax = 0
  LengthMin = 0
  Placement1 = pos=(0,0,-34) rot=(0,0,1;0rad)
  Placement2 = pos=(0,187.334,351.344) rot=(-0.57735,0.57735,0.57735;4.18879rad)
  Reference1 = -> Assembly [M6x70_Screw.Edge53,M6x70_Screw.Edge53]
  Reference2 = -> Assembly [Stand.Pocket001.Face13,Stand.Pocket001.Face13]
FEATURE [App::FeaturePython] Joint001  label="Revolute001"  # Assembly joint (typed FeaturePython)
  Activated = true
  AngleMax = 0
  AngleMin = 0
  Detach1 = false
  Detach2 = false
  Distance = 0
  Distance2 = 0
  EnableAngleMax = false
  EnableAngleMin = false
  EnableLengthMax = false
  EnableLengthMin = false
  JointType = 1 (Revolute)
  LengthMax = 0
  LengthMin = 0
  Placement1 = pos=(0,0,-34) rot=(0,0,1;0rad)
  Placement2 = pos=(0,199.784,270.092) rot=(-0.57735,0.57735,0.57735;4.18879rad)
  Reference1 = -> Assembly [M6x70_Screw001.Edge53,M6x70_Screw001.Edge53]
  Reference2 = -> Assembly [Stand.Pocket001.Face12,Stand.Pocket001.Face12]
FEATURE [App::FeaturePython] Joint002  label="Fixed"  # Assembly joint (typed FeaturePython)
  Activated = true
  AngleMax = 0
  AngleMin = 0
  Detach1 = false
  Detach2 = false
  Distance = 0
  Distance2 = 0
  EnableAngleMax = false
  EnableAngleMin = false
  EnableLengthMax = false
  EnableLengthMin = false
  JointType = 0 (Fixed)
  LengthMax = 0
  LengthMin = 0
  Placement1 = pos=(-100.78,-34.9255,15) rot=(-1,0,0;4.71239rad)
  Placement2 = pos=(0,0,-68.8) rot=(0,0,1;0rad)
  Reference1 = -> Assembly [Vessel_Holder.Pocket004.Edge5,Vessel_Holder.Pocket004.Edge5]
  Reference2 = -> Assembly [M6x70_Screw001.Edge55,M6x70_Screw001.Edge55]
FEATURE [App::FeaturePython] Joint004  label="Fixed002"  # Assembly joint (typed FeaturePython)
  Activated = true
  AngleMax = 0
  AngleMin = 0
  Detach1 = false
  Detach2 = false
  Distance = 0
  Distance2 = 0
  EnableAngleMax = false
  EnableAngleMin = false
  EnableLengthMax = false
  EnableLengthMin = false
  JointType = 0 (Fixed)
  LengthMax = 0
  LengthMin = 0
  Placement1 = pos=(-2.13e-14,-8.9e-15,20) rot=(0,-1,0;3.14159rad)
  Placement2 = pos=(0,3.6e-15,30) rot=(0,0,1;0rad)
  Reference1 = -> Assembly [Pressure_Vessel.Revolution003.Face1,Pressure_Vessel.Revolution003.Face1]
  Reference2 = -> Assembly [Vessel_Holder.Edge22,Vessel_Holder.Edge22]
FEATURE [App::Link] Presure_Lever  label="Presure Lever001"
  LinkPlacement = pos=(0.1,-36.069,422.145) rot=(0.704345,-0.704345,0.0883;2.96545rad)
  LinkedObject = -> Body002
  Placement = pos=(0.1,-36.069,422.145) rot=(0.704345,-0.704345,0.0883;2.96545rad)
FEATURE [App::FeaturePython] Joint005  label="Revolute002"  # Assembly joint (typed FeaturePython)
  Activated = true
  AngleMax = 0
  AngleMin = 0
  Detach1 = false
  Detach2 = false
  Distance = 0
  Distance2 = 0
  EnableAngleMax = false
  EnableAngleMin = false
  EnableLengthMax = false
  EnableLengthMin = false
  JointType = 1 (Revolute)
  LengthMax = 0
  LengthMin = 0
  Placement1 = pos=(-233.967,17.5,13.4636) rot=(1,0,0;1.5708rad)
  Placement2 = pos=(0,0,-51.4) rot=(0,0,1;0rad)
  Reference1 = -> Assembly [Presure_Lever.Pocket003.Face41,Presure_Lever.Pocket003.Face41]
  Reference2 = -> Assembly [M6x70_Screw.Face23,M6x70_Screw.Face23]
FEATURE [App::FeaturePython] Joint006  label="Slider"  # Assembly joint (typed FeaturePython)
  Activated = true
  AngleMax = 0
  AngleMin = 0
  Detach1 = false
  Detach2 = false
  Distance = 0
  Distance2 = 0
  EnableAngleMax = false
  EnableAngleMin = false
  EnableLengthMax = false
  EnableLengthMin = false
  JointType = 3 (Slider)
  LengthMax = 0
  LengthMin = 0
  Offset2 = pos=(0,0,0) rot=(0,0,1;1.5708rad)
  Placement1 = pos=(0,1.24e-14,61.2441) rot=(0,0,1;0rad)
  Placement2 = pos=(-2.84e-14,-8.9e-15,30.0382) rot=(1,0,0;3.14159rad)
  Reference1 = -> Assembly [Pressure_Vessel.Revolution003.Face20,Pressure_Vessel.Revolution003.Face20]
  Reference2 = -> Assembly [Plunger.Fillet004.Face1,Plunger.Fillet004.Face1]
FEATURE [App::FeaturePython] Joint007  label="Revolute003"  # Assembly joint (typed FeaturePython)
  Activated = true
  AngleMax = 0
  AngleMin = 0
  Detach1 = false
  Detach2 = false
  Distance = 0
  Distance2 = 0
  EnableAngleMax = false
  EnableAngleMin = false
  EnableLengthMax = false
  EnableLengthMin = false
  JointType = 1 (Revolute)
  LengthMax = 0
  LengthMin = 0
  Placement1 = pos=(-158.2,12.5,21.0121) rot=(1,0,0;1.5708rad)
  Placement2 = pos=(0,0,0.385) rot=(0,0,1;0rad)
  Reference1 = -> Assembly [Presure_Lever.Pocket003.Edge70,Presure_Lever.Pocket003.Edge70]
  Reference2 = -> Assembly [M12x45_Screw001.Edge19,M12x45_Screw001.Edge19]
FEATURE [App::FeaturePython] Joint008  label="Fixed003"  # Assembly joint (typed FeaturePython)
  Activated = true
  AngleMax = 0
  AngleMin = 0
  Detach1 = false
  Detach2 = false
  Distance = 0
  Distance2 = 0
  EnableAngleMax = false
  EnableAngleMin = false
  EnableLengthMax = false
  EnableLengthMin = false
  JointType = 0 (Fixed)
  LengthMax = 0
  LengthMin = 0
  Placement1 = pos=(0,0,0.385) rot=(0,0,1;0rad)
  Placement2 = pos=(-4.26e-14,4.995,106.2) rot=(0.57735,0.57735,-0.57735;2.0944rad)
  Reference1 = -> Assembly [M12x45_Screw001.Edge19,M12x45_Screw001.Edge19]
  Reference2 = -> Assembly [Plunger.Fillet004.Edge19,Plunger.Fillet004.Edge19]
FEATURE [Assembly::JointGroup] Joints
  Group = -> [GroundedJoint,Joint,Joint001,Joint002,Joint004,Joint005,Joint006,Joint007,Joint008]
FEATURE [Assembly::AssemblyObject] Assembly
  Group = -> [Joints,Stand,GroundedJoint,Pressure_Vessel,Vessel_Holder,Plunger,M12x45_Screw001,M6x70_Screw,M6x70_Screw001,Joint,Joint001,Joint002,Joint004,Presure_Lever,Joint005,Joint006,Joint007,Joint008]
  Origin = -> Origin005
  Type = Assembly
